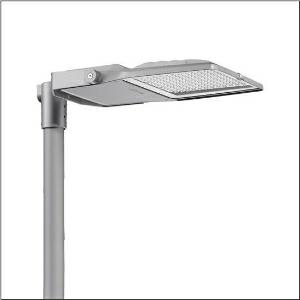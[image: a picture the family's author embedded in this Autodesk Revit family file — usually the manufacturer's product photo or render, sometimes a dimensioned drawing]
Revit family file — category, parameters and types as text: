
# Revit family: floodlight_fl_21_midi___pl33t_5xa7785e2f3a_9b27
name_source: partatom
category: Lighting Fixtures
units: mm (PartAtom-declared; Revit-internal decimal feet)

## family parameters
Cut with Voids When Loaded = No
Host = Face
Light Source = No
Part Type = Normal
Room Calculation Point = No
Round Connector Dimension = Use Diameter
Shared = No

## types (1)
- --- (1 x LED, 26630 lm, 212.4 W, 3000K)
    Apparent Load = 212 VA
    CIE Flux Codes = 26 75 99 100 100
    Color Rendering = 70
    Color Temperature = 3000K
    Default Elevation = 1800 mm
    Description = Floodlight FL 21 midi, floodlight, primary light control with lens, of PMMA, primary optical cover: protective disc, of toughened safety glass, transparent, light distribution: PL33T, light emission: direct distribution, installation type: surface-mounted, LED, High Power LED, rated luminous flux: 26.630lm, luminous efficacy: 125lm/W, light colour: 730, colour temperature: 3000K, control gear: Smart Interface (Zhaga), control: flexible luminous flux parameterisation, time-dependent luminous flux control, constant luminous flux control, overheat protection, pre-setting: logarithmic dimming characteristic, with terminal, 6-pole, mains connection: 220..240V, AC, 50/60Hz, start of lifetime: 212W, end of service life: 231W, reduction: 95W, luminaire housing, of diecast aluminium, powder-coated, Siteco® metallic grey (DB 702S), corrosivity category C5 mid according to DIN EN ISO 12944, suitable for swimming pools, chlorine-resistant, sealing non-destructively replaceable, please order mast flange separately, mast bracket, of steel, galvanised, powder-coated, Siteco® metallic grey (DB 702S), Smart Interface above, protection rating (complete): IP66, insulation class (complete): insulation class II (safety insulation), certification: CE, ENEC, VDE, protection symbol: D, impact resistance: IK08, permissible operating ambient temperature: -20..+40°C, permissible operating ambient temperature for outdoor applications: -40..+50°C, standard: DIN EN 12944, LABS conformity tested according to VDMA 24364:2018-05, packaging unit: 1 piece

Light Distribution: PL33T
    Height = 76 mm
    Lamp = 1 x LED
    Lamp Light Flux = 26630 lm
    Lamp Power = 212.4 W
    Lamp count = 1
    Length = 657 mm
    Luminous efficacy = 125 lm/W
    Manufacturer = Siteco
    ModVariant = No
    Model = 5XA7785E2F3A
    Number of Poles = 1
    OnlyDefault = Yes
    Power Factor = 1
    Product Name = Floodlight FL 21 midi | PL33T
    Product group = floodlight | pylon annexe
    ProductGroupID = 6201
    Protection Class = Protection class II
    Protection Degree = IP 66
    RLX_Detail_Level = 1
    RLX_Emergency_Light_Flux = 0 lm
    RLX_Emergency_Type = 0
    RLX_Emergency_Type_DB = No
    RlxData = <blob elided: 153417 chars, md5=abb6e967>
    Socket = socket
    Standby Power = 0 W
    System Light Flux = 26630 lm
    System Power = 212 W
    Type Comments = factory setting: luminous flux: 100 % | dim-lin: 254 | 710 mA
    Type Image = l_1007123.jpg
    URL = http://relux.com
    VarID = @adj_172061
    Voltage = 0 V
    Weight = 0.00 kg
    Width = 442 mm

## geometry (parser evidence)
native form markers: Blend x4, Sweep x13
no freeform markers — native parametric forms only
